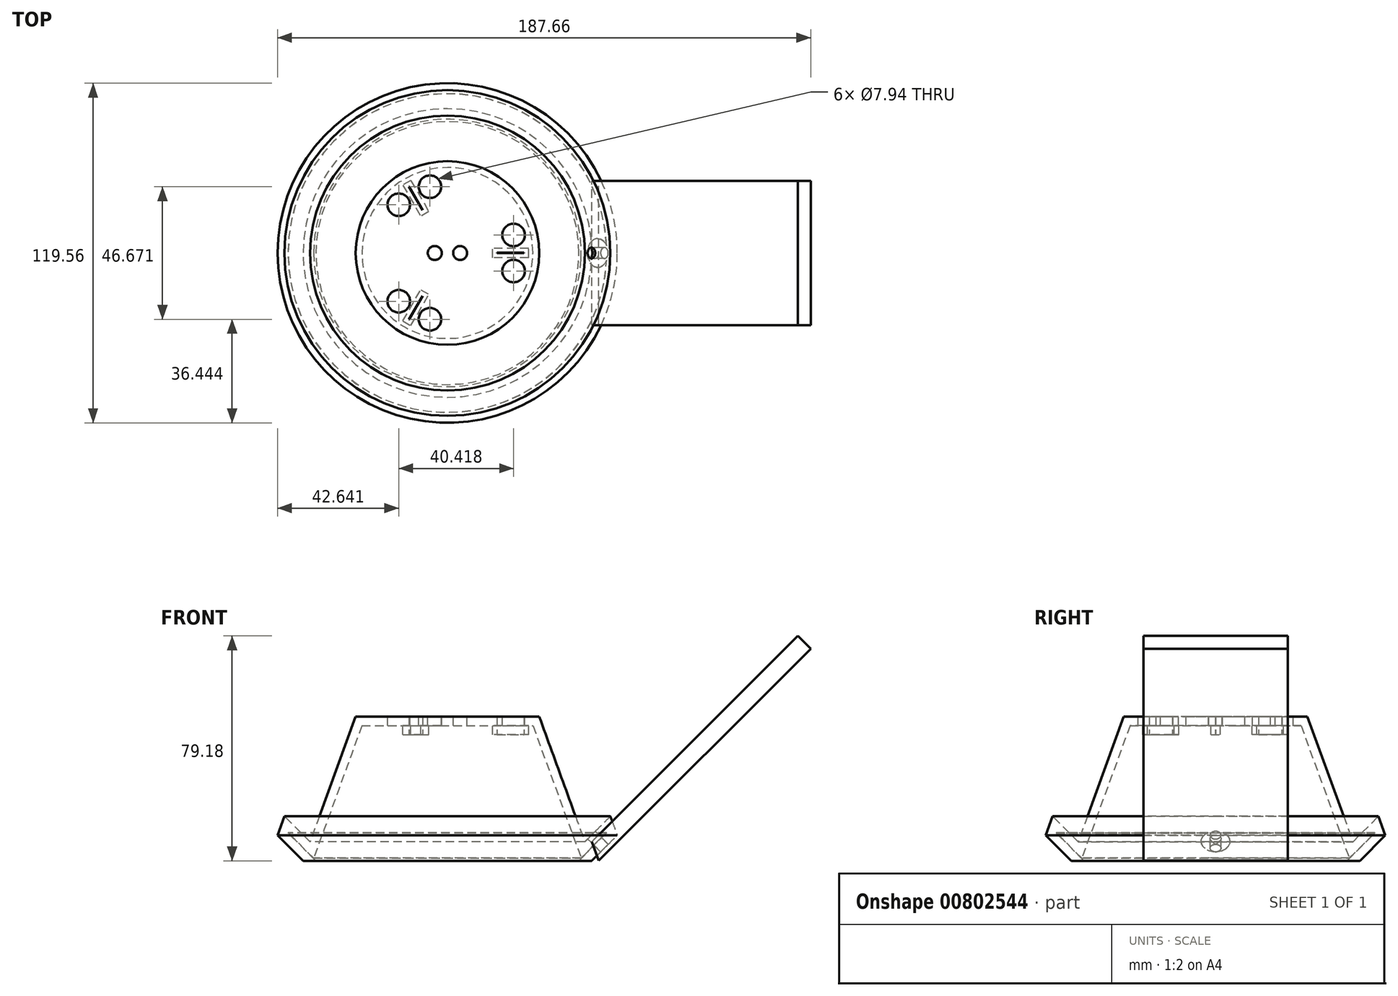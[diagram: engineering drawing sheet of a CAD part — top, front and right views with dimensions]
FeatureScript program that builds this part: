
annotation { "Feature Type Name" : "Feature", "Feature Type Description" : "" }
export const myFeature = defineFeature(function(context is Context, id is Id, definition is map)
    precondition{}
    {
        {
            var Q0;
            Q0=qCreatedBy(makeId("Front.planeOp"),FACE);
            var sketch = newSketch(context, id + "F0", { "sketchPlane" : qUnion([Q0])});
            skLineSegment(sketch, "E0", {"start": v(32.3, 94.92) * mm, "end": v(48.37, 50.8) * mm});
            skLineSegment(sketch, "E1", {"start": v(48.37, 50.8) * mm, "end": v(57.35, 59.78) * mm});
            skLineSegment(sketch, "E2", {"start": v(57.35, 59.78) * mm, "end": v(59.78, 53.1) * mm});
            skLineSegment(sketch, "E3", {"start": v(59.78, 53.1) * mm, "end": v(50.8, 44.12) * mm});
            skLineSegment(sketch, "E4", {"start": v(0, 53.57) * mm, "end": v(0, 0) * mm});
            skLineSegment(sketch, "E5", {"start": v(32.3, 94.92) * mm, "end": v(0, 94.92) * mm});
            skLineSegment(sketch, "E6", {"start": v(0, 94.92) * mm, "end": v(0, 44.12) * mm});
            skLineSegment(sketch, "E7", {"start": v(0, 44.12) * mm, "end": v(50.8, 44.12) * mm});
            skSolve(sketch);
        }
        {
            var Q0;
            Q0=makeQuery(id+"F0.imprint","IMPRINT",FACE,{"disambiguationData":[TD([[makeQuery(id+"F0.imprint","IMPRINT",EDGE,{"derivedFrom":sQuery(id+"F0.wireOp",EDGE,"E0")}),-1.0]])]});
            var Q1;
            {var subQ0=sQuery(id+"F0.wireOp",EDGE,"E1");Q1=makeQuery(id+"F0.imprint","IMPRINT",FACE,{"disambiguationData":[TD([[makeQuery(id+"F0.imprint","IMPRINT",EDGE,{"derivedFrom":subQ0}),-1.0]])]});}
            var Q2;
            Q2=sQuery(id+"F0.wireOp",EDGE,"E4");
            revolve(context, id + "F1", {"surfaceOperationType" : NewSurfaceOperationType.NEW, "entities" : qUnion([Q0, Q1]), "axis" : qUnion([Q2]), "revolveType" : RevolveType.FULL});
        }
        {
            var Q0;
            Q0=qCreatedBy(makeId("Front.planeOp"),FACE);
            var sketch = newSketch(context, id + "F2", { "sketchPlane" : qUnion([Q0])});
            skLineSegment(sketch, "E8.0", {"start": v(127.88, 118.72) * mm, "end": v(53.3, 44.14) * mm});
            skLineSegment(sketch, "E8.1", {"start": v(50.8, 50.8) * mm, "end": v(123.3, 123.3) * mm});
            skLineSegment(sketch, "E8.2", {"start": v(123.3, 123.3) * mm, "end": v(127.88, 118.72) * mm});
            skPoint(sketch, "E8.3", {"position": v(125.59, 121) * mm});
            skLineSegment(sketch, "E9", {"start": v(50.8, 50.8) * mm, "end": v(53.3, 44.14) * mm});
            skSolve(sketch);
        }
        {
            var Q0;
            Q0=makeQuery(id+"F2.imprint","IMPRINT",FACE,{"disambiguationData":[TD([[makeQuery(id+"F2.imprint","IMPRINT",EDGE,{"derivedFrom":sQuery(id+"F2.wireOp",EDGE,"E8.0")}),-1.0]])]});
            extrude(context, id + "F3", {"entities" : qUnion([Q0]), "depth" : 25.4 * mm, "offsetDistance" : 25.4 * mm, "hasSecondDirection" : true, "secondDirectionOppositeDirection" : true, "secondDirectionDepth" : 25.4 * mm});
        }
        {
            var Q0;
            Q0=makeQuery(id+"F3.opExtrude","SWEPT_FACE",FACE,{"disambiguationData":[OSD([sQuery(id+"F2.wireOp",EDGE,"E8.1")])]});
            var sketch = newSketch(context, id + "F4", { "sketchPlane" : qUnion([Q0])});
            skEllipse(sketch, "E10.0", {"center": v(0, 35.92) * mm, "majorRadius": 48.37 * mm, "minorRadius": 34.2 * mm, "majorAxis": v(-1, 0), "construction": true});
            skEllipse(sketch, "E10.1", {"center": v(0, 42.27) * mm, "majorRadius": 57.35 * mm, "minorRadius": 40.55 * mm, "majorAxis": v(-1, 0), "construction": true});
            skLineSegment(sketch, "E11", {"start": v(0, 64.03) * mm, "end": v(0, 82.82) * mm, "construction": true});
            skCircle(sketch, "E12", {"center": v(0, 73.42) * mm, "radius": 1.9 * mm});
            skSolve(sketch);
        }
        {
            var Q0;
            Q0=qSketchRegion(id+"F4",true);
            extrude(context, id + "F5", {"entities" : qUnion([Q0]), "operationType" : NewBodyOperationType.REMOVE, "endBound" : BoundingType.UP_TO_NEXT, "oppositeDirection" : true, "depth" : 25.4 * mm, "offsetDistance" : 25.4 * mm, "hasSecondDirection" : true, "secondDirectionBound" : SecondDirectionBoundingType.UP_TO_NEXT, "secondDirectionOppositeDirection" : false, "secondDirectionDepth" : 25.4 * mm});
        }
        {
            var Q0;
            Q0=makeQuery(id+"F1.opRevolve","SWEPT_FACE",FACE,{"disambiguationData":[OSD([sQuery(id+"F0.wireOp",EDGE,"E7")])]});
            shell(context, id + "F6", {"entities" : qUnion([Q0]), "thickness" : 3.17 * mm});
        }
        {
            var Q0;
            Q0=makeQuery(id+"F1.opRevolve","SWEPT_FACE",FACE,{"disambiguationData":[OSD([sQuery(id+"F0.wireOp",EDGE,"E5")])]});
            var sketch = newSketch(context, id + "F7", { "sketchPlane" : qUnion([Q0])});
            skCircle(sketch, "E13", {"center": v(-4.46, 0) * mm, "radius": 2.47 * mm});
            skCircle(sketch, "E14", {"center": v(4.47, 0) * mm, "radius": 2.47 * mm});
            skSolve(sketch);
        }
        {
            var Q0;
            Q0 = qSketchRegion(id + "F7", true);
            extrude(context, id + "F8", {"entities" : qUnion([Q0]), "operationType" : NewBodyOperationType.REMOVE, "endBound" : BoundingType.UP_TO_NEXT, "oppositeDirection" : true, "depth" : 25.4 * mm, "offsetDistance" : 25.4 * mm});
        }
        {
            var Q0;
            Q0=makeQuery(id+"F1.opRevolve","SWEPT_FACE",FACE,{"disambiguationData":[OSD([sQuery(id+"F0.wireOp",EDGE,"E5")])]});
            var sketch = newSketch(context, id + "F9", { "sketchPlane" : qUnion([Q0])});
            skLineSegment(sketch, "E15", {"start": v(0, 0) * mm, "end": v(-16.15, 27.98) * mm, "construction": true});
            skLineSegment(sketch, "E16", {"start": v(0, 0) * mm, "end": v(32.3, 0) * mm, "construction": true});
            skLineSegment(sketch, "E17", {"start": v(0, 0) * mm, "end": v(-16.15, -27.98) * mm, "construction": true});
            skCircle(sketch, "E18", {"center": v(0, 0) * mm, "radius": 24.13 * mm, "construction": true});
            skCircle(sketch, "E19", {"center": v(-6.14, -23.34) * mm, "radius": 3.97 * mm});
            skCircle(sketch, "E20", {"center": v(-17.14, -16.99) * mm, "radius": 3.97 * mm});
            skCircle(sketch, "E21.1.0", {"center": v(23.28, -6.35) * mm, "radius": 3.97 * mm});
            skCircle(sketch, "E21.1.1", {"center": v(23.28, 6.35) * mm, "radius": 3.97 * mm});
            skCircle(sketch, "E21.2.0", {"center": v(-6.14, 23.34) * mm, "radius": 3.97 * mm});
            skCircle(sketch, "E21.2.1", {"center": v(-17.14, 16.99) * mm, "radius": 3.97 * mm});
            skSolve(sketch);
        }
        {
            var Q0;
            Q0=makeQuery(id+"F9.imprint","IMPRINT",FACE,{"disambiguationData":[TD([[makeQuery(id+"F9.imprint","IMPRINT",EDGE,{"derivedFrom":sQuery(id+"F9.wireOp",EDGE,"RapGbSY8-IpOW-W7Cr-I6qc-ZG4xxbcdLVoa")}),1.0]])]});
            var Q1;
            Q1=makeQuery(id+"F9.imprint","IMPRINT",FACE,{"disambiguationData":[TD([[makeQuery(id+"F9.imprint","IMPRINT",EDGE,{"derivedFrom":sQuery(id+"F9.wireOp",EDGE,"IGuVjlWC-YWjh-J5nc-Mawc-mcWyPe0ibYVq")}),1.0]])]});
            var Q2;
            Q2=makeQuery(id+"F9.imprint","IMPRINT",FACE,{"disambiguationData":[TD([[makeQuery(id+"F9.imprint","IMPRINT",EDGE,{"derivedFrom":sQuery(id+"F9.wireOp",EDGE,"F3LzENUP-gJWh-AGhM-4yzn-LWY1Z7Q8ePyD")}),1.0]])]});
            var Q3;
            Q3=makeQuery(id+"F9.imprint","IMPRINT",FACE,{"disambiguationData":[TD([[makeQuery(id+"F9.imprint","IMPRINT",EDGE,{"derivedFrom":sQuery(id+"F9.wireOp",EDGE,"3u7ExzTy-9fGH-4HWB-yVm0-lmGXTGqtbzzD")}),1.0]])]});
            var Q4;
            Q4=makeQuery(id+"F9.imprint","IMPRINT",FACE,{"disambiguationData":[TD([[makeQuery(id+"F9.imprint","IMPRINT",EDGE,{"derivedFrom":sQuery(id+"F9.wireOp",EDGE,"E19")}),1.0]])]});
            var Q5;
            Q5=makeQuery(id+"F9.imprint","IMPRINT",FACE,{"disambiguationData":[TD([[makeQuery(id+"F9.imprint","IMPRINT",EDGE,{"derivedFrom":sQuery(id+"F9.wireOp",EDGE,"E20")}),1.0]])]});
            var Q6;
            Q6=makeQuery(id+"F9.imprint","IMPRINT",FACE,{"disambiguationData":[TD([[makeQuery(id+"F9.imprint","IMPRINT",EDGE,{"derivedFrom":sQuery(id+"F9.wireOp",EDGE,"E21.2.1")}),1.0]])]});
            var Q7;
            Q7=makeQuery(id+"F9.imprint","IMPRINT",FACE,{"disambiguationData":[TD([[makeQuery(id+"F9.imprint","IMPRINT",EDGE,{"derivedFrom":sQuery(id+"F9.wireOp",EDGE,"E21.2.0")}),1.0]])]});
            var Q8;
            Q8=makeQuery(id+"F9.imprint","IMPRINT",FACE,{"disambiguationData":[TD([[makeQuery(id+"F9.imprint","IMPRINT",EDGE,{"derivedFrom":sQuery(id+"F9.wireOp",EDGE,"E21.1.1")}),1.0]])]});
            var Q9;
            Q9=makeQuery(id+"F9.imprint","IMPRINT",FACE,{"disambiguationData":[TD([[makeQuery(id+"F9.imprint","IMPRINT",EDGE,{"derivedFrom":sQuery(id+"F9.wireOp",EDGE,"E21.1.0")}),1.0]])]});
            extrude(context, id + "F10", {"entities" : qUnion([Q0, Q1, Q2, Q3, Q4, Q5, Q6, Q7, Q8, Q9]), "operationType" : NewBodyOperationType.REMOVE, "endBound" : BoundingType.UP_TO_NEXT, "oppositeDirection" : true, "depth" : 25.4 * mm, "offsetDistance" : 25.4 * mm});
        }
        {
            var Q0;
            Q0=makeQuery(id+"F6.opShell","OFFSET_FACE",FACE,{"disambiguationData":[OSD([sQuery(id+"F0.wireOp",EDGE,"E5")])]});
            var sketch = newSketch(context, id + "F11", { "sketchPlane" : qUnion([Q0])});
            skLineSegment(sketch, "E22", {"start": v(1.4, 0) * mm, "end": v(77.6, 0) * mm, "construction": true});
            skLineSegment(sketch, "E23.bottom", {"start": v(28.58, 1.65) * mm, "end": v(15.88, 1.65) * mm});
            skLineSegment(sketch, "E23.top", {"start": v(28.58, -1.65) * mm, "end": v(15.88, -1.65) * mm});
            skLineSegment(sketch, "E23.left", {"start": v(28.57, 1.65) * mm, "end": v(28.57, -1.65) * mm});
            skLineSegment(sketch, "E23.right", {"start": v(15.88, 1.65) * mm, "end": v(15.88, -1.65) * mm});
            skLineSegment(sketch, "E24.1.0", {"start": v(-12.86, 25.57) * mm, "end": v(-6.5, 14.57) * mm});
            skLineSegment(sketch, "E24.1.1", {"start": v(-9.37, 12.92) * mm, "end": v(-6.5, 14.57) * mm});
            skLineSegment(sketch, "E24.1.2", {"start": v(-15.72, 23.92) * mm, "end": v(-9.37, 12.92) * mm});
            skLineSegment(sketch, "E24.1.3", {"start": v(-15.72, 23.92) * mm, "end": v(-12.86, 25.57) * mm});
            skLineSegment(sketch, "E24.2.0", {"start": v(-15.72, -23.92) * mm, "end": v(-9.37, -12.92) * mm});
            skLineSegment(sketch, "E24.2.1", {"start": v(-6.5, -14.57) * mm, "end": v(-9.37, -12.92) * mm});
            skLineSegment(sketch, "E24.2.2", {"start": v(-12.86, -25.57) * mm, "end": v(-6.5, -14.57) * mm});
            skLineSegment(sketch, "E24.2.3", {"start": v(-12.86, -25.57) * mm, "end": v(-15.72, -23.92) * mm});
            skPoint(sketch, "E24.center", {"position": v(0, 0) * mm});
            skSolve(sketch);
        }
        {
            var Q0;
            Q0=makeQuery(id+"F11.imprint","IMPRINT",FACE,{"disambiguationData":[TD([[makeQuery(id+"F11.imprint","IMPRINT",EDGE,{"derivedFrom":sQuery(id+"F11.wireOp",EDGE,"E23.bottom")}),1.0]])]});
            var Q1;
            Q1=makeQuery(id+"F11.imprint","IMPRINT",FACE,{"disambiguationData":[TD([[makeQuery(id+"F11.imprint","IMPRINT",EDGE,{"derivedFrom":sQuery(id+"F11.wireOp",EDGE,"E24.1.0")}),-1.0]])]});
            var Q2;
            Q2=makeQuery(id+"F11.imprint","IMPRINT",FACE,{"disambiguationData":[TD([[makeQuery(id+"F11.imprint","IMPRINT",EDGE,{"derivedFrom":sQuery(id+"F11.wireOp",EDGE,"E24.2.0")}),-1.0]])]});
            extrude(context, id + "F12", {"entities" : qUnion([Q0, Q1, Q2]), "operationType" : NewBodyOperationType.ADD, "depth" : 3.17 * mm, "offsetDistance" : 25.4 * mm});
        }
        {
            var Q0;
            Q0=makeQuery(id+"F12.opExtrude","CAP_FACE",FACE,{"disambiguationData":[OSD([sQuery(id+"F11.wireOp",EDGE,"E24.2.0"),sQuery(id+"F11.wireOp",EDGE,"E24.2.1"),sQuery(id+"F11.wireOp",EDGE,"E24.2.2"),sQuery(id+"F11.wireOp",EDGE,"E24.2.3")])],"isStart":false});
            var sketch = newSketch(context, id + "F13", { "sketchPlane" : qUnion([Q0])});
            skLineSegment(sketch, "E25.0", {"start": v(32.3, 0) * mm, "end": v(0, 0) * mm, "construction": true});
            skLineSegment(sketch, "E26", {"start": v(17.48, 0.05) * mm, "end": v(26.97, 0.05) * mm});
            skLineSegment(sketch, "E27", {"start": v(26.97, 0.05) * mm, "end": v(26.97, -0.05) * mm});
            skLineSegment(sketch, "E28", {"start": v(26.97, -0.05) * mm, "end": v(17.48, -0.05) * mm});
            skLineSegment(sketch, "E29", {"start": v(17.48, -0.05) * mm, "end": v(17.48, 0.05) * mm});
            skLineSegment(sketch, "E30.1.0", {"start": v(-13.44, 23.39) * mm, "end": v(-8.7, 15.16) * mm});
            skLineSegment(sketch, "E30.1.1", {"start": v(-8.7, 15.16) * mm, "end": v(-8.78, 15.1) * mm});
            skLineSegment(sketch, "E30.1.2", {"start": v(-8.78, 15.1) * mm, "end": v(-13.53, 23.34) * mm});
            skLineSegment(sketch, "E30.1.3", {"start": v(-13.53, 23.34) * mm, "end": v(-13.44, 23.39) * mm});
            skLineSegment(sketch, "E30.2.0", {"start": v(-13.53, -23.34) * mm, "end": v(-8.78, -15.1) * mm});
            skLineSegment(sketch, "E30.2.1", {"start": v(-8.78, -15.1) * mm, "end": v(-8.7, -15.16) * mm});
            skLineSegment(sketch, "E30.2.2", {"start": v(-8.7, -15.16) * mm, "end": v(-13.44, -23.39) * mm});
            skLineSegment(sketch, "E30.2.3", {"start": v(-13.44, -23.39) * mm, "end": v(-13.53, -23.34) * mm});
            skPoint(sketch, "E30.center", {"position": v(0, 0) * mm});
            skSolve(sketch);
        }
        {
            var Q0;
            Q0=makeQuery(id+"F13.imprint","IMPRINT",FACE,{"disambiguationData":[TD([[makeQuery(id+"F13.imprint","IMPRINT",EDGE,{"derivedFrom":sQuery(id+"F13.wireOp",EDGE,"E26")}),-1.0]])]});
            var Q1;
            Q1=makeQuery(id+"F13.imprint","IMPRINT",FACE,{"disambiguationData":[TD([[makeQuery(id+"F13.imprint","IMPRINT",EDGE,{"derivedFrom":sQuery(id+"F13.wireOp",EDGE,"E30.2.0")}),-1.0]])]});
            var Q2;
            Q2=makeQuery(id+"F13.imprint","IMPRINT",FACE,{"disambiguationData":[TD([[makeQuery(id+"F13.imprint","IMPRINT",EDGE,{"derivedFrom":sQuery(id+"F13.wireOp",EDGE,"E30.1.0")}),-1.0]])]});
            extrude(context, id + "F14", {"entities" : qUnion([Q0, Q1, Q2]), "operationType" : NewBodyOperationType.REMOVE, "oppositeDirection" : true, "depth" : 25.4 * mm, "offsetDistance" : 25.4 * mm});
        }
    });
